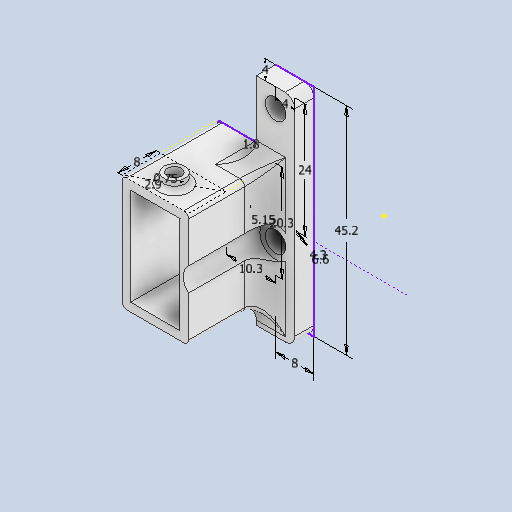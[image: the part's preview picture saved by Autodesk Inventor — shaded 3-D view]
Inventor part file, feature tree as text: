
AUTODESK INVENTOR PART (.ipt)
format: ipt  version: 2023 (Build 270158000, 158)  size: 354,304 bytes
history: native  units: mm
features: extrude x7, fillet x4, sketch x2, hole x1
ambient origin geometry x8: Origin, YZ Plane, XZ Plane, XY Plane, X Axis, Y Axis, Z Axis, Center Point
bodies: Solid1 (feature_tree)
feature tree (14):
  extrude  "Extrusion1"  Depth=20.0mm TaperAngle=0.0deg
  extrude  "Extrusion2"  Depth=4.3mm
  hole  "Hole1"  [1 undecoded]
  fillet  "Fillet1"  Radius=24.0mm
  fillet  "Fillet3"  Radius=4.3mm
  sketch  "Sketch2"  dims[d8=4.0mm d9=0.0mm d10=4.0mm d11=4.0mm d12=24.0mm d13=4.3mm d14=6.0mm d15=4.0mm d16=2.0mm d17=90.0deg d18=5.0mm d19=20.594885mm d20=4.3mm d22=1.0mm d23=8.0mm d24=2.9mm d25=0.75mm d26=2.0mm d27=0.0mm d28=2.0mm d29=1.0mm d30=2.0mm d31=0.0mm d32=6.6mm d33=20.0mm d34=0.0mm d35=4.3mm d36=4.0mm d37=0.0mm d38=4.0mm d39=0.0mm]
  extrude  "Extrusion3"  Depth=1.0mm
  fillet  "Fillet4"  Radius=8.0mm
  fillet  "Fillet5"  Radius=2.9mm
  extrude  "Extrusion4"  Depth=4.3mm
  extrude  "Extrusion5"  Depth=4.3mm TaperAngle=0.0deg
  extrude  "Extrusion6"  Depth=4.3mm
  extrude  "Extrusion7"  Depth=1.0mm
  sketch  "Sketch1"  dims[d0=8.0mm d1=45.2mm d2=5.15mm d3=10.3mm d4=20.3mm d5=1.8mm d6=20.0mm d7=0.0mm]
note: 1 required parameter value undecoded (feature->parameter linkage not recoverable at this tier; creation-order binding heuristic only, values carry confidence <= 0.55)
